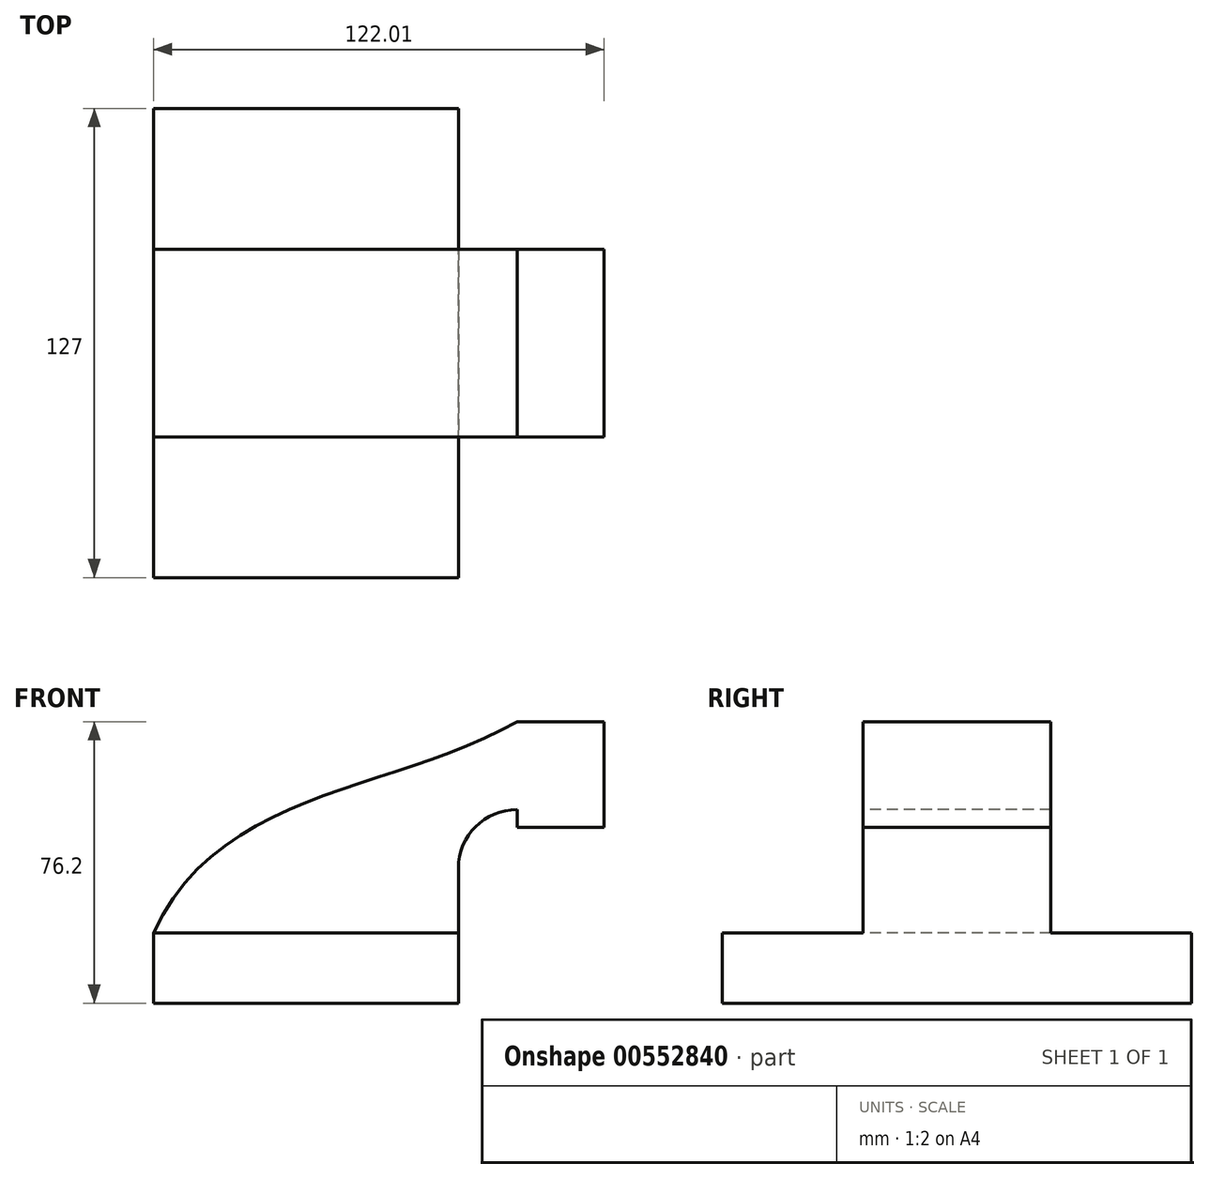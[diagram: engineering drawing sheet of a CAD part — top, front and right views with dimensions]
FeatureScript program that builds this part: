
annotation { "Feature Type Name" : "Feature", "Feature Type Description" : "" }
export const myFeature = defineFeature(function(context is Context, id is Id, definition is map)
    precondition{}
    {
        {
            var Q0;
            Q0=qCreatedBy(makeId("Front.planeOp"),FACE);
            var sketch = newSketch(context, id + "F0", { "sketchPlane" : qUnion([Q0])});
            skLineSegment(sketch, "E0.bottom", {"start": v(-140.7, -34.03) * mm, "end": v(-223.25, -34.03) * mm});
            skLineSegment(sketch, "E0.top", {"start": v(-140.7, -53.08) * mm, "end": v(-223.25, -53.08) * mm});
            skLineSegment(sketch, "E0.left", {"start": v(-140.7, -34.03) * mm, "end": v(-140.7, -53.08) * mm});
            skLineSegment(sketch, "E0.right", {"start": v(-223.25, -34.03) * mm, "end": v(-223.25, -53.08) * mm});
            skLineSegment(sketch, "E1.bottom", {"start": v(-74.03, 23.12) * mm, "end": v(-124.83, 23.12) * mm});
            skLineSegment(sketch, "E1.top", {"start": v(-74.03, -5.45) * mm, "end": v(-124.83, -5.45) * mm});
            skLineSegment(sketch, "E1.left", {"start": v(-74.03, 23.12) * mm, "end": v(-74.03, -5.45) * mm});
            skLineSegment(sketch, "E1.right", {"start": v(-124.83, 23.12) * mm, "end": v(-124.83, -5.45) * mm});
            skLineSegment(sketch, "E2", {"start": v(-140.7, -34.03) * mm, "end": v(-140.7, -16.55) * mm});
            skArc(sketch, "E3", {"start": v(-140.7, -16.55) * mm, "mid": v(-136.05, -5.33) * mm, "end": v(-124.83, -0.68) * mm});
            skLineSegment(sketch, "E4", {"start": v(-124.83, -0.68) * mm, "end": v(-101.25, -0.68) * mm});
            skLineSegment(sketch, "E5.0", {"start": v(-124.83, 18.37) * mm, "end": v(-101.25, 18.37) * mm});
            skArc(sketch, "E5.1", {"start": v(-159.75, -16.55) * mm, "mid": v(-149.52, 8.14) * mm, "end": v(-124.83, 18.37) * mm});
            skLineSegment(sketch, "E5.2", {"start": v(-159.75, -24.03) * mm, "end": v(-159.75, -16.55) * mm});
            skLineSegment(sketch, "E6", {"start": v(-101.24, -5.45) * mm, "end": v(-101.24, 23.12) * mm});
            skFitSpline(sketch, "E7", {"points": [v(-223.25, -34.03) * mm, v(-124.83, 23.12) * mm], "startDerivative": vector(54.6, 118.3) * mm, "endDerivative": vector(98.42, 57.15) * mm});
            skSolve(sketch);
        }
        {
            var Q0;
            Q0=makeQuery(id+"F0.imprint","IMPRINT",FACE,{"disambiguationData":[TD([[makeQuery(id+"F0.imprint","IMPRINT",EDGE,{"derivedFrom":sQuery(id+"F0.wireOp",EDGE,"E0.bottom")}),1.0]])]});
            extrude(context, id + "F1", {"entities" : qUnion([Q0]), "endBound" : BoundingType.SYMMETRIC, "depth" : 127 * mm, "offsetDistance" : 25.4 * mm});
        }
        {
            var Q0;
            Q0=makeQuery(id+"F0.imprint","IMPRINT",FACE,{"disambiguationData":[TD([[makeQuery(id+"F0.imprint","IMPRINT",EDGE,{"derivedFrom":sQuery(id+"F0.wireOp",EDGE,"E0.bottom")}),-1.0]])]});
            var Q1;
            {var subQ6=sQuery(id+"F0.wireOp",EDGE,"E6");Q1=makeQuery(id+"F0.imprint","IMPRINT",FACE,{"disambiguationData":[TD([[makeQuery(id+"F0.imprint","IMPRINT",EDGE,{"derivedFrom":subQ6}),1.0]])]});}
            extrude(context, id + "F2", {"entities" : qUnion([Q0, Q1]), "operationType" : NewBodyOperationType.ADD, "endBound" : BoundingType.SYMMETRIC, "oppositeDirection" : true, "depth" : 50.8 * mm, "offsetDistance" : 25.4 * mm});
        }
    });
